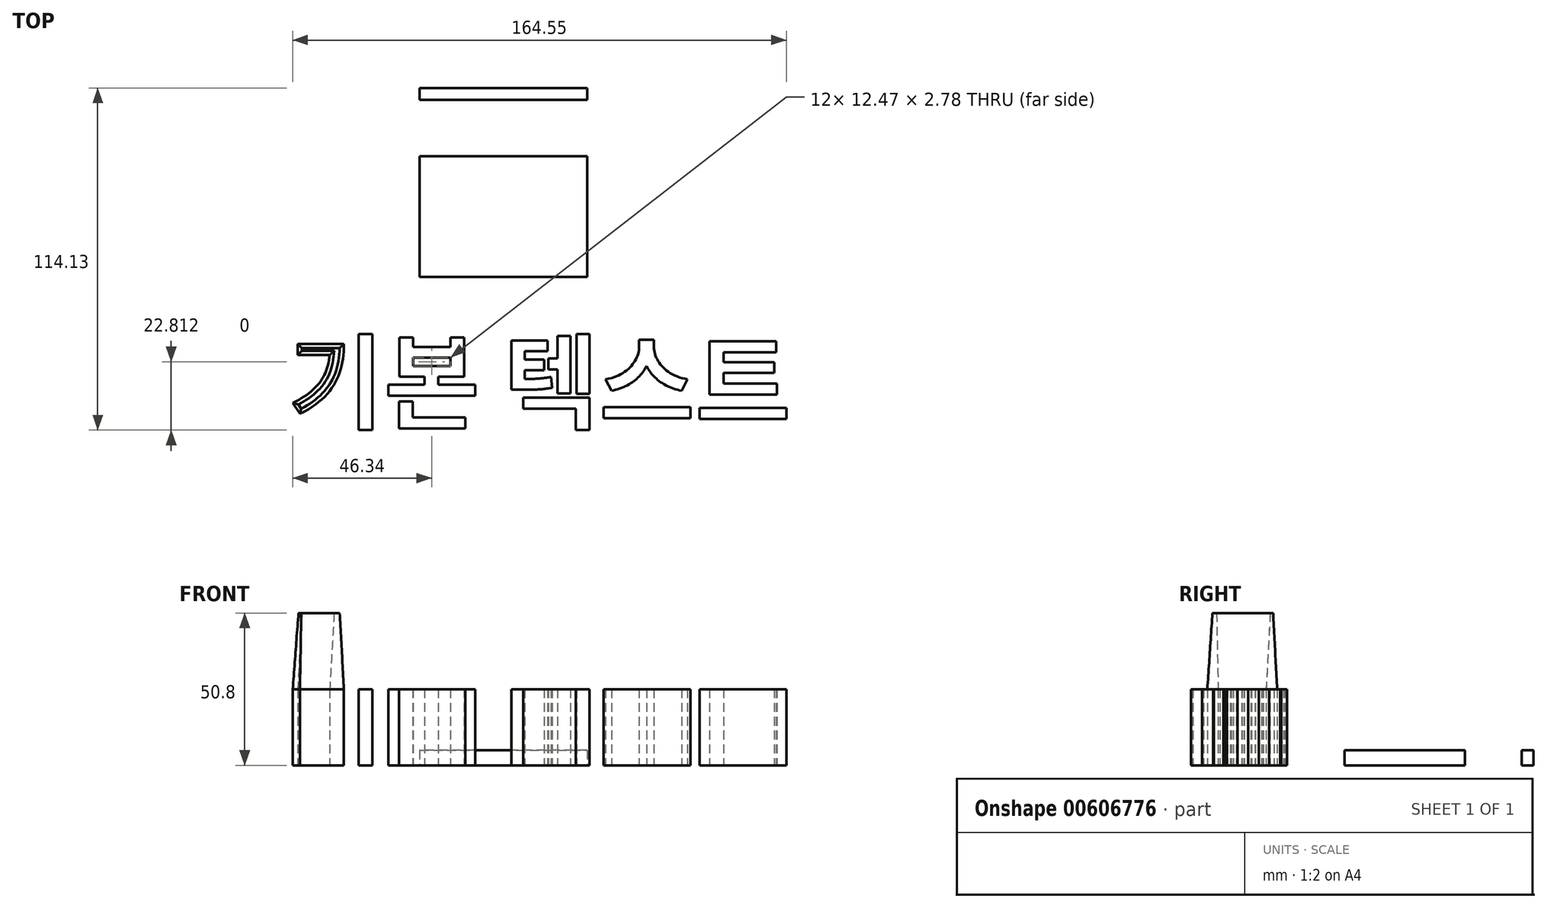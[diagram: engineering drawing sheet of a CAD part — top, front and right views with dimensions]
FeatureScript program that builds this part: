
annotation { "Feature Type Name" : "Feature", "Feature Type Description" : "" }
export const myFeature = defineFeature(function(context is Context, id is Id, definition is map)
    precondition{}
    {
        {
            var Q0;
            Q0=qCreatedBy(makeId("Top.planeOp"),FACE);
            var sketch = newSketch(context, id + "F0", { "sketchPlane" : qUnion([Q0])});
            skLineSegment(sketch, "E0.bottom", {"start": v(-21.42, 36.39) * mm, "end": v(34.44, 36.39) * mm});
            skLineSegment(sketch, "E0.top", {"start": v(-21.42, 40.3) * mm, "end": v(34.44, 40.3) * mm});
            skLineSegment(sketch, "E0.left", {"start": v(-21.42, 36.39) * mm, "end": v(-21.42, 40.3) * mm});
            skLineSegment(sketch, "E0.right", {"start": v(34.44, 36.39) * mm, "end": v(34.44, 40.3) * mm});
            skLineSegment(sketch, "E1.bottom", {"start": v(34.44, -22.7) * mm, "end": v(-21.42, -22.7) * mm});
            skLineSegment(sketch, "E1.top", {"start": v(34.44, 17.5) * mm, "end": v(-21.42, 17.5) * mm});
            skLineSegment(sketch, "E1.left", {"start": v(34.44, -22.7) * mm, "end": v(34.44, 17.5) * mm});
            skLineSegment(sketch, "E1.right", {"start": v(-21.42, -22.7) * mm, "end": v(-21.42, 17.5) * mm});
            skSolve(sketch);
        }
        {
            var Q0;
            Q0 = qSketchRegion(id + "F0", true);
            extrude(context, id + "F1", {"entities" : qUnion([Q0]), "depth" : 5 * mm, "offsetDistance" : 25.4 * mm});
        }
        {
            var Q0;
            Q0=qCreatedBy(makeId("Top.planeOp"),FACE);
            var sketch = newSketch(context, id + "F2", { "sketchPlane" : qUnion([Q0])});
            skText(sketch, "E2", { "text": "기본 텍스트\n", "fontName": "NotoSansCJKkr-Bold.otf"});
            const initialGuessF2  = {"E2": [-0.06526, -0.0708, 1, 0, 0.025]};
            skSetInitialGuess(sketch, initialGuessF2);
            skSolve(sketch);
        }
        {
            var Q0;
            Q0 = qSketchRegion(id + "F2", true);
            extrude(context, id + "F3", {"entities" : qUnion([Q0]), "depth" : 25.4 * mm, "offsetDistance" : 25.4 * mm});
        }
        {
            var Q0;
            Q0=makeQuery(id+"F3.opExtrude","CAP_FACE",FACE,{"disambiguationData":[OSD([sQuery(id+"F2.wireOp",EDGE,"E2.sketch_text.stroke-0"),sQuery(id+"F2.wireOp",EDGE,"E2.sketch_text.stroke-1"),sQuery(id+"F2.wireOp",EDGE,"E2.sketch_text.stroke-2"),sQuery(id+"F2.wireOp",EDGE,"E2.sketch_text.stroke-3"),sQuery(id+"F2.wireOp",EDGE,"E2.sketch_text.stroke-4"),sQuery(id+"F2.wireOp",EDGE,"E2.sketch_text.stroke-5")])],"isStart":false});
            extrude(context, id + "F4", {"entities" : qUnion([Q0]), "operationType" : NewBodyOperationType.ADD, "depth" : 25.4 * mm, "offsetDistance" : 25.4 * mm, "hasDraft" : true, "draftAngle" : 3 * degree, "draftPullDirection" : true});
        }
    });
